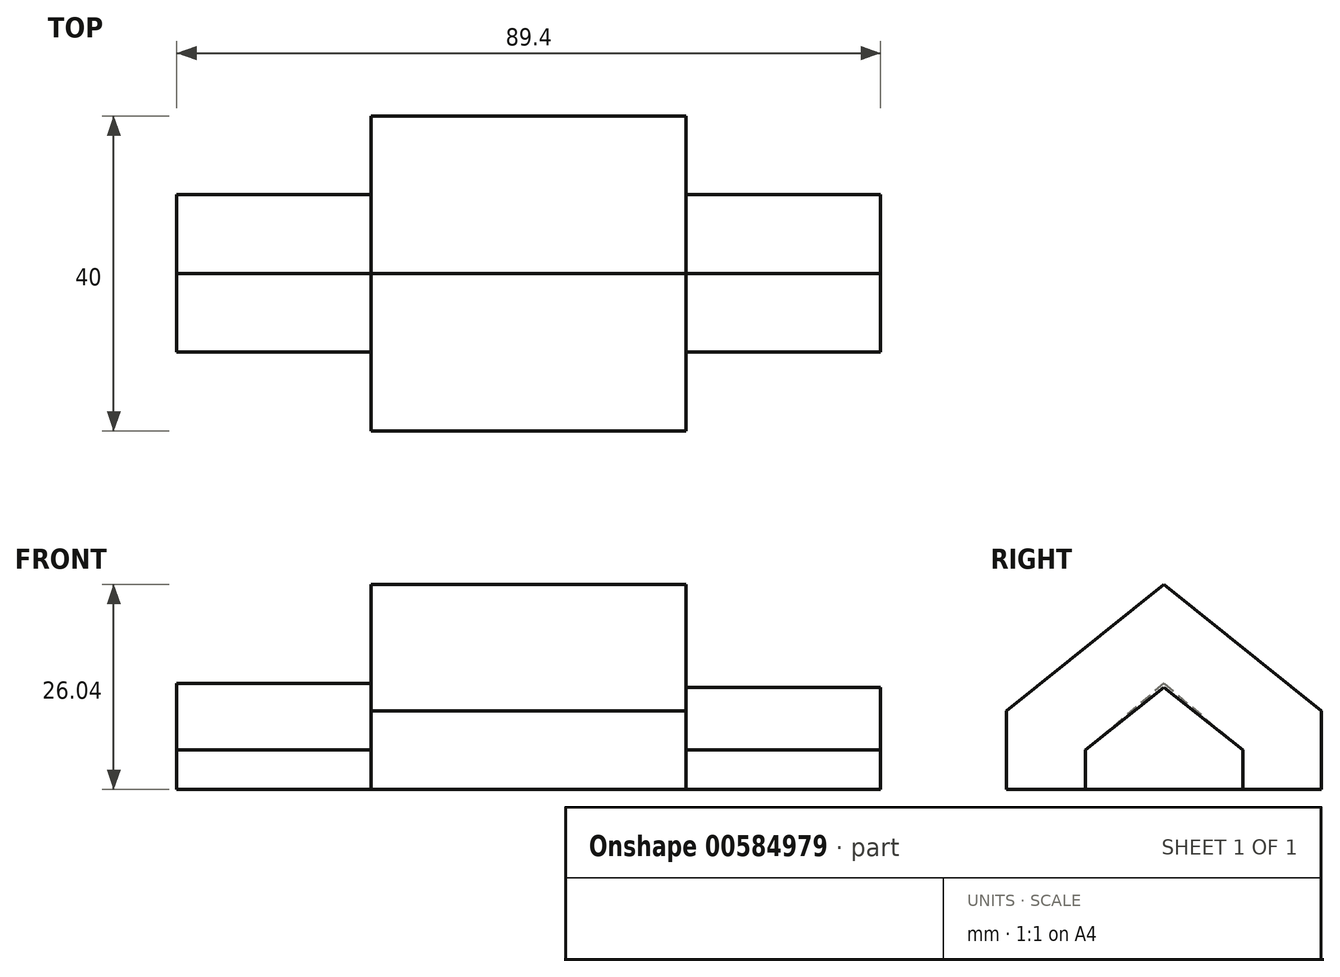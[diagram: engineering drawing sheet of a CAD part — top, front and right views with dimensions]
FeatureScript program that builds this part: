
annotation { "Feature Type Name" : "Feature", "Feature Type Description" : "" }
export const myFeature = defineFeature(function(context is Context, id is Id, definition is map)
    precondition{}
    {
        {
            var Q0;
            Q0=qCreatedBy(makeId("Top.planeOp"),FACE);
            var sketch = newSketch(context, id + "F0", { "sketchPlane" : qUnion([Q0])});
            skLineSegment(sketch, "E0", {"start": v(-20, 15) * mm, "end": v(-20, 25) * mm});
            skLineSegment(sketch, "E1", {"start": v(-20, 25) * mm, "end": v(20, 25) * mm});
            skLineSegment(sketch, "E2", {"start": v(20, 25) * mm, "end": v(20, 15) * mm});
            skLineSegment(sketch, "E3", {"start": v(20, 15) * mm, "end": v(44.7, 15) * mm});
            skLineSegment(sketch, "E4", {"start": v(44.7, 15) * mm, "end": v(44.7, -5) * mm});
            skLineSegment(sketch, "E5", {"start": v(44.7, -5) * mm, "end": v(20, -5) * mm});
            skLineSegment(sketch, "E6", {"start": v(20, -5) * mm, "end": v(20, -15) * mm});
            skLineSegment(sketch, "E7", {"start": v(20, -15) * mm, "end": v(-20, -15) * mm});
            skLineSegment(sketch, "E8", {"start": v(-20, -15) * mm, "end": v(-20, -5) * mm});
            skLineSegment(sketch, "E9", {"start": v(-20, -5) * mm, "end": v(-44.7, -5) * mm});
            skLineSegment(sketch, "E10", {"start": v(-44.7, -5) * mm, "end": v(-44.7, 15) * mm});
            skLineSegment(sketch, "E11", {"start": v(-44.7, 15) * mm, "end": v(-20, 15) * mm});
            skPoint(sketch, "E12", {"position": v(0, -15) * mm});
            skPoint(sketch, "E13", {"position": v(-4, -15) * mm});
            skPoint(sketch, "E14", {"position": v(4, -15) * mm});
            skLineSegment(sketch, "E15", {"start": v(-20, 15) * mm, "end": v(-20, -5) * mm});
            skLineSegment(sketch, "E16", {"start": v(20, 15) * mm, "end": v(20, -5) * mm});
            skSolve(sketch);
        }
        {
            var Q0;
            Q0=makeQuery(id+"F0.imprint","IMPRINT",FACE,{"disambiguationData":[TD([[makeQuery(id+"F0.imprint","IMPRINT",EDGE,{"derivedFrom":sQuery(id+"F0.wireOp",EDGE,"E0")}),-1.0]])]});
            extrude(context, id + "F1", {"entities" : qUnion([Q0]), "depth" : 10 * mm, "offsetDistance" : 25 * mm});
        }
        {
            var Q0;
            Q0 = qSketchRegion(id + "F0", true);
            extrude(context, id + "F2", {"entities" : qUnion([Q0]), "operationType" : NewBodyOperationType.ADD, "depth" : 5 * mm, "offsetDistance" : 25 * mm});
        }
        {
            var Q0;
            Q0=makeQuery(id+"F1.opExtrude","SWEPT_FACE",FACE,{"disambiguationData":[OSD([sQuery(id+"F0.wireOp",EDGE,"E2"),sQuery(id+"F0.wireOp",EDGE,"E6"),sQuery(id+"F0.wireOp",EDGE,"E16")])]});
            cPlane(context, id + "F3", {"entities" : qUnion([Q0]), "cplaneType" : CPlaneType.OFFSET, "offset" : 0 * mm, "width" : 150 * mm, "height" : 150 * mm});
        }
        {
            var Q0;
            Q0=qCreatedBy(id+"F3.planeOp",FACE);
            var sketch = newSketch(context, id + "F4", { "sketchPlane" : qUnion([Q0])});
            skLineSegment(sketch, "E17.0", {"start": v(15, 5) * mm, "end": v(-5, 5) * mm});
            skLineSegment(sketch, "E18", {"start": v(-5, 5) * mm, "end": v(5, 12.95) * mm});
            skLineSegment(sketch, "E19", {"start": v(5, 12.95) * mm, "end": v(15, 5) * mm});
            skLineSegment(sketch, "E20.0", {"start": v(25, 10) * mm, "end": v(-15, 10) * mm});
            skLineSegment(sketch, "E21", {"start": v(-15, 10) * mm, "end": v(5, 26.04) * mm});
            skLineSegment(sketch, "E22", {"start": v(5, 26.04) * mm, "end": v(25, 10) * mm});
            skSolve(sketch);
        }
        {
            var Q0;
            {var subQ0=sQuery(id+"F4.wireOp",EDGE,"E17.0");Q0=makeQuery(id+"F4.imprint","IMPRINT",FACE,{"disambiguationData":[TD([[makeQuery(id+"F4.imprint","IMPRINT",EDGE,{"derivedFrom":subQ0}),-1.0]])]});}
            var Q1;
            {var subQ0=sQuery(id+"F4.wireOp",EDGE,"E19");var subQ1=sQuery(id+"F4.wireOp",EDGE,"E18");var subQ2=makeQuery(id+"F4.imprint","INTERSECT",VERTEX,{"derivedFrom":[subQ1,subQ0]});Q1=makeQuery(id+"F4.imprint","IMPRINT",FACE,{"disambiguationData":[TD([[makeQuery(id+"F4.imprint","IMPRINT",EDGE,{"disambiguationData":[TD([[subQ2,1.0]])],"derivedFrom":subQ1}),-1.0]])]});}
            extrude(context, id + "F5", {"entities" : qUnion([Q0, Q1]), "operationType" : NewBodyOperationType.ADD, "depth" : 24.7 * mm, "offsetDistance" : 25 * mm});
        }
        {
            var Q0;
            {var subQ6=sQuery(id+"F4.wireOp",EDGE,"E21");Q0=makeQuery(id+"F4.imprint","IMPRINT",FACE,{"disambiguationData":[TD([[makeQuery(id+"F4.imprint","IMPRINT",EDGE,{"derivedFrom":subQ6}),-1.0]])]});}
            var Q1;
            {var subQ0=sQuery(id+"F4.wireOp",EDGE,"E19");var subQ1=sQuery(id+"F4.wireOp",EDGE,"E18");var subQ2=makeQuery(id+"F4.imprint","INTERSECT",VERTEX,{"derivedFrom":[subQ1,subQ0]});Q1=makeQuery(id+"F4.imprint","IMPRINT",FACE,{"disambiguationData":[TD([[makeQuery(id+"F4.imprint","IMPRINT",EDGE,{"disambiguationData":[TD([[subQ2,1.0]])],"derivedFrom":subQ1}),-1.0]])]});}
            extrude(context, id + "F6", {"entities" : qUnion([Q0, Q1]), "operationType" : NewBodyOperationType.ADD, "oppositeDirection" : true, "depth" : 40 * mm, "offsetDistance" : 25 * mm});
        }
        {
            var Q0;
            Q0=makeQuery(id+"F6.boolean.opBoolean","MERGE",FACE,{"derivedFrom":[makeQuery(id+"F1.opExtrude","SWEPT_FACE",FACE,{"disambiguationData":[OSD([sQuery(id+"F0.wireOp",EDGE,"E0"),sQuery(id+"F0.wireOp",EDGE,"E8"),sQuery(id+"F0.wireOp",EDGE,"E15")])]}),makeQuery(id+"F6.opExtrude","CAP_FACE",FACE,{"disambiguationData":[OSD([sQuery(id+"F4.wireOp",EDGE,"E20.0"),sQuery(id+"F4.wireOp",EDGE,"E21"),sQuery(id+"F4.wireOp",EDGE,"E22")])],"isStart":false})]});
            cPlane(context, id + "F7", {"entities" : qUnion([Q0]), "cplaneType" : CPlaneType.OFFSET, "offset" : 0 * mm, "width" : 150 * mm, "height" : 150 * mm});
        }
        {
            var Q0;
            Q0=qCreatedBy(id+"F7.planeOp",FACE);
            var sketch = newSketch(context, id + "F8", { "sketchPlane" : qUnion([Q0])});
            skLineSegment(sketch, "E23.0", {"start": v(5, 5) * mm, "end": v(-15, 5) * mm});
            skLineSegment(sketch, "E24", {"start": v(-15, 5) * mm, "end": v(-5, 13.46) * mm});
            skLineSegment(sketch, "E25", {"start": v(-5, 13.46) * mm, "end": v(5, 5) * mm});
            skSolve(sketch);
        }
        {
            var Q0;
            Q0=makeQuery(id+"F8.imprint","IMPRINT",FACE,{"disambiguationData":[TD([[makeQuery(id+"F8.imprint","IMPRINT",EDGE,{"derivedFrom":sQuery(id+"F8.wireOp",EDGE,"E23.0")}),-1.0]])]});
            extrude(context, id + "F9", {"entities" : qUnion([Q0]), "operationType" : NewBodyOperationType.ADD, "depth" : 24.7 * mm, "offsetDistance" : 25 * mm});
        }
    });
